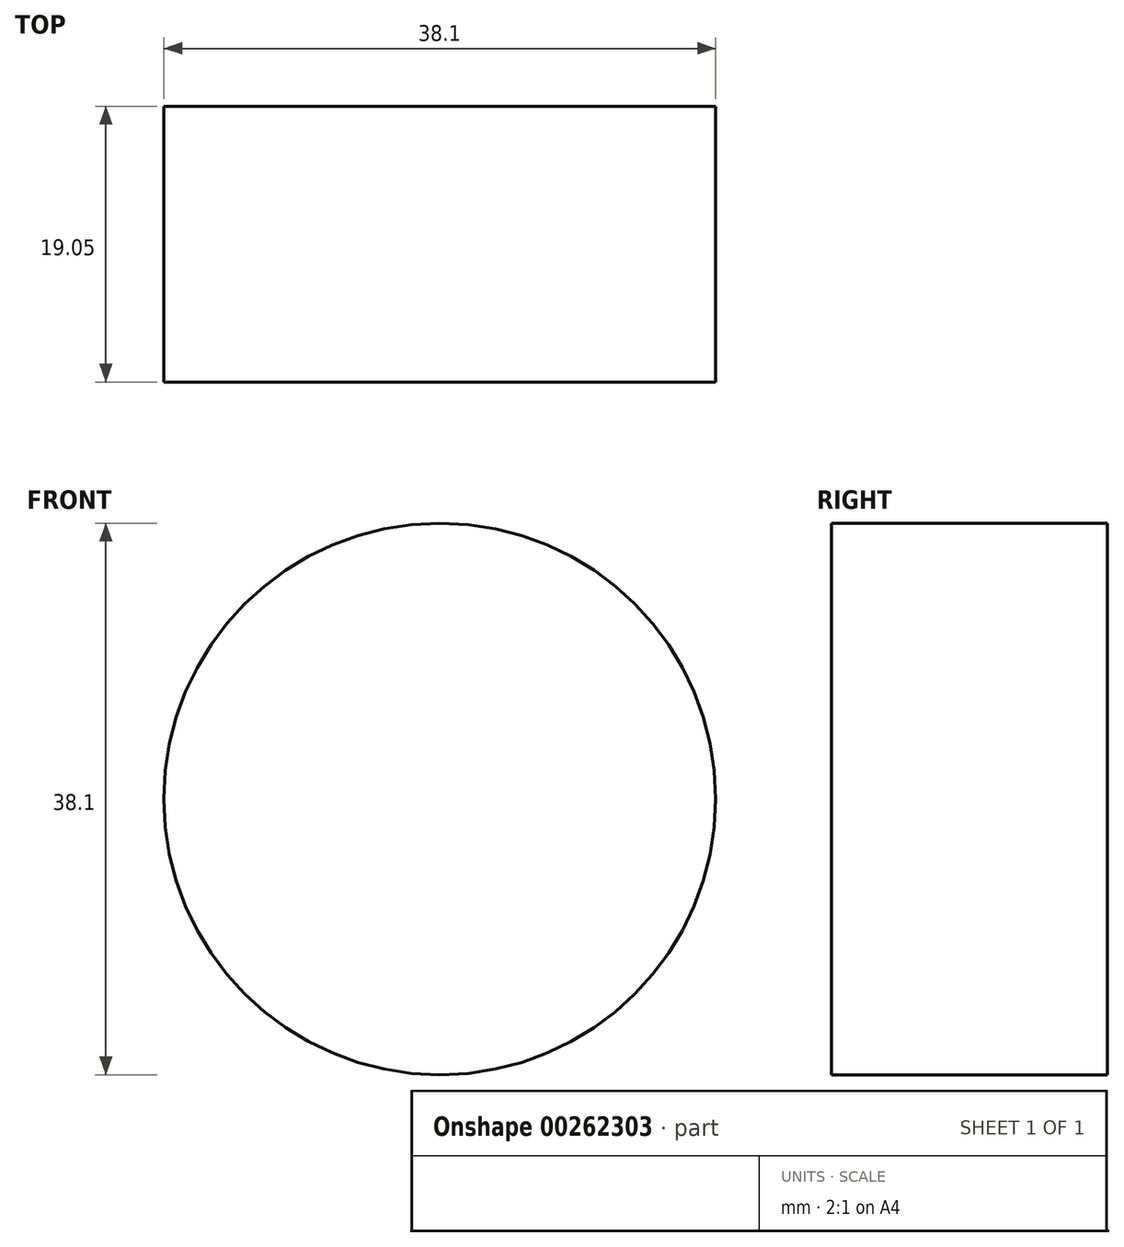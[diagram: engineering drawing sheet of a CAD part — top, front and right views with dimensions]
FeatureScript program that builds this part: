
annotation { "Feature Type Name" : "Feature", "Feature Type Description" : "" }
export const myFeature = defineFeature(function(context is Context, id is Id, definition is map)
    precondition{}
    {
        {
            var Q0;
            Q0=qCreatedBy(makeId("Front.planeOp"),FACE);
            var sketch = newSketch(context, id + "F0", { "sketchPlane" : qUnion([Q0])});
            skCircle(sketch, "E0", {"center": v(0, 0) * mm, "radius": 19.05 * mm});
            skSolve(sketch);
        }
        {
            var Q0;
            Q0 = qSketchRegion(id + "F0", true);
            extrude(context, id + "F1", {"entities" : qUnion([Q0]), "depth" : 19.05 * mm});
        }
    });
